# Revit family: Furniture_Other_Sjobergs_Workbench_Elite_1500
name_source: partatom
category: Furniture
revit_build: Autodesk Revit 2017 (Build: 20160225_1515(x64)
units: mm (PartAtom-declared; Revit-internal decimal feet)

## family parameters
Always vertical = Yes
Cut with Voids When Loaded = No
OmniClass Number = 23.40.70.14
OmniClass Title = Retail and Commercial Equipment and Furnishings
Room Calculation Point = No
Shared = No
Work Plane-Based = No

## types (1)
- 35001 Workbench Elite 1500 + SM03 Cabinet
    AssetType = Movable
    BIMObjectName = Furniture_Other_Sjobergs_Workbench_Elite_1500
    Brand = Sjöbergs
    Category = Hobby
    Collection = Elite
    Color = Wooden
    Constituents = Elite 1500 (article n. 33246) + SM03 (article n. 33457)
    ConvergoRefNr = 0184-2005-0015-SE
    Cost = 0 $
    Description = Sjöbergs Elite is both heavier and smarter than any other bench on the market. Designed and manufactured for professionals by professionals. Solid beech construction. Treated with oil. The powerful Elite bench together with our smart accessories make it a perfect workplace.
    DurationUnit = Year
    EANNumber = 7316703246151 + 7316703457038
    Features = The bench consists of cabinets and drawers SM03. 4-pack steel hooks are included.
    Finish = Countertop in solid beech with double notch rows. Treated with oil.
    IfcExportAs = IfcFurnishingElementType
    IfcExportType = TABLE
    MainColor = Wooden
    Manufacturer = Sjöbergs
    ManufacturerName = Sjöbergs
    ManufacturerURL = https://www.sjobergs.se
    Material = Wood, metal
    Model = 35001 Workbench Elite 1500 + SM03 Cabinet
    ModelReference = 35001
    NBSDescription = School art, design and technology tables and workbenches;
    NBSReference = 45-35-20/320
    Name = Sjobergs_Workbench_Elite_1500
    NominalDepth = 741 mm
    NominalHeight = 901 mm
    NominalLength = 1517 mm
    ProductDatasheet = https://www.sjobergs.se
    ProductInformation = Sjöbergs Elite is both heavier and smarter than any other bench on the market. Designed and manufactured for professionals by professionals. Solid beech construction. Treated with oil. The powerful Elite bench together with our smart accessories make it a perfect workplace.
    Shape = Sculptured
    Size = 1515x740x900 mm
    TableMainMaterial = Beech
    TableSecondaryMaterial = Black Metal
    URL = https://www.sjobergs.se
    Uniclass2 = Pr_40_50_21
    Uniclass2015Description = Desks, Tables And Worktops
    Uniclass2015Reference = Pr_40_50_21_76
    Version = 1
    VersionDate = 26/06/2020
    WarrantyDurationUnit = Year
    Weight = 125.0 kg

## geometry (parser evidence)
native form markers: Sweep x7
no freeform markers — native parametric forms only
